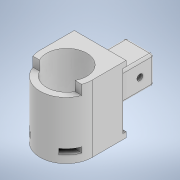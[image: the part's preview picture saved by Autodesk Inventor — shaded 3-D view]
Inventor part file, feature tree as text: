
AUTODESK INVENTOR PART (.ipt)
format: ipt  version: 2020.2 (Build 242310000, 310)  size: 402,432 bytes
history: native  units: mm
features: sketch x10, extrude x7, fillet x4, hole x3
ambient origin geometry x8: Origin, YZ Plane, XZ Plane, XY Plane, X Axis, Y Axis, Z Axis, Center Point
bodies: Solido1 (feature_tree)
feature tree (24):
  extrude  "Estrusione1"  Depth=18.0mm
  extrude  "Estrusione2"  Depth=40.0mm TaperAngle=0.0deg
  extrude  "Estrusione3"  Depth=62.5mm
  extrude  "Estrusione10"  Depth=48.4mm
  hole  "Foro4"  [1 undecoded]
  hole  "Foro5"  [1 undecoded]
  fillet  "Raccordo1"  [1 undecoded]
  fillet  "Raccordo2"  Radius=37.5mm
  fillet  "Raccordo3"  Radius=55.5mm
  extrude  "Estrusione16"  Depth=3.0mm
  hole  "Foro9"  [1 undecoded]
  extrude  "Estrusione17"  Depth=26.0mm
  fillet  "Raccordo5"  Radius=40.0mm
  extrude  "Estrusione18"  Depth=13.0mm
  sketch  "Schizzo1"
  sketch  "Schizzo2"
  sketch  "Schizzo3"
  sketch  "Schizzo14"
  sketch  "Schizzo15"
  sketch  "Schizzo16"
  sketch  "Schizzo26"
  sketch  "Schizzo27"
  sketch  "Schizzo28"
  sketch  "Schizzo29"
note: 4 required parameter values undecoded (feature->parameter linkage not recoverable at this tier; creation-order binding heuristic only, values carry confidence <= 0.55)
